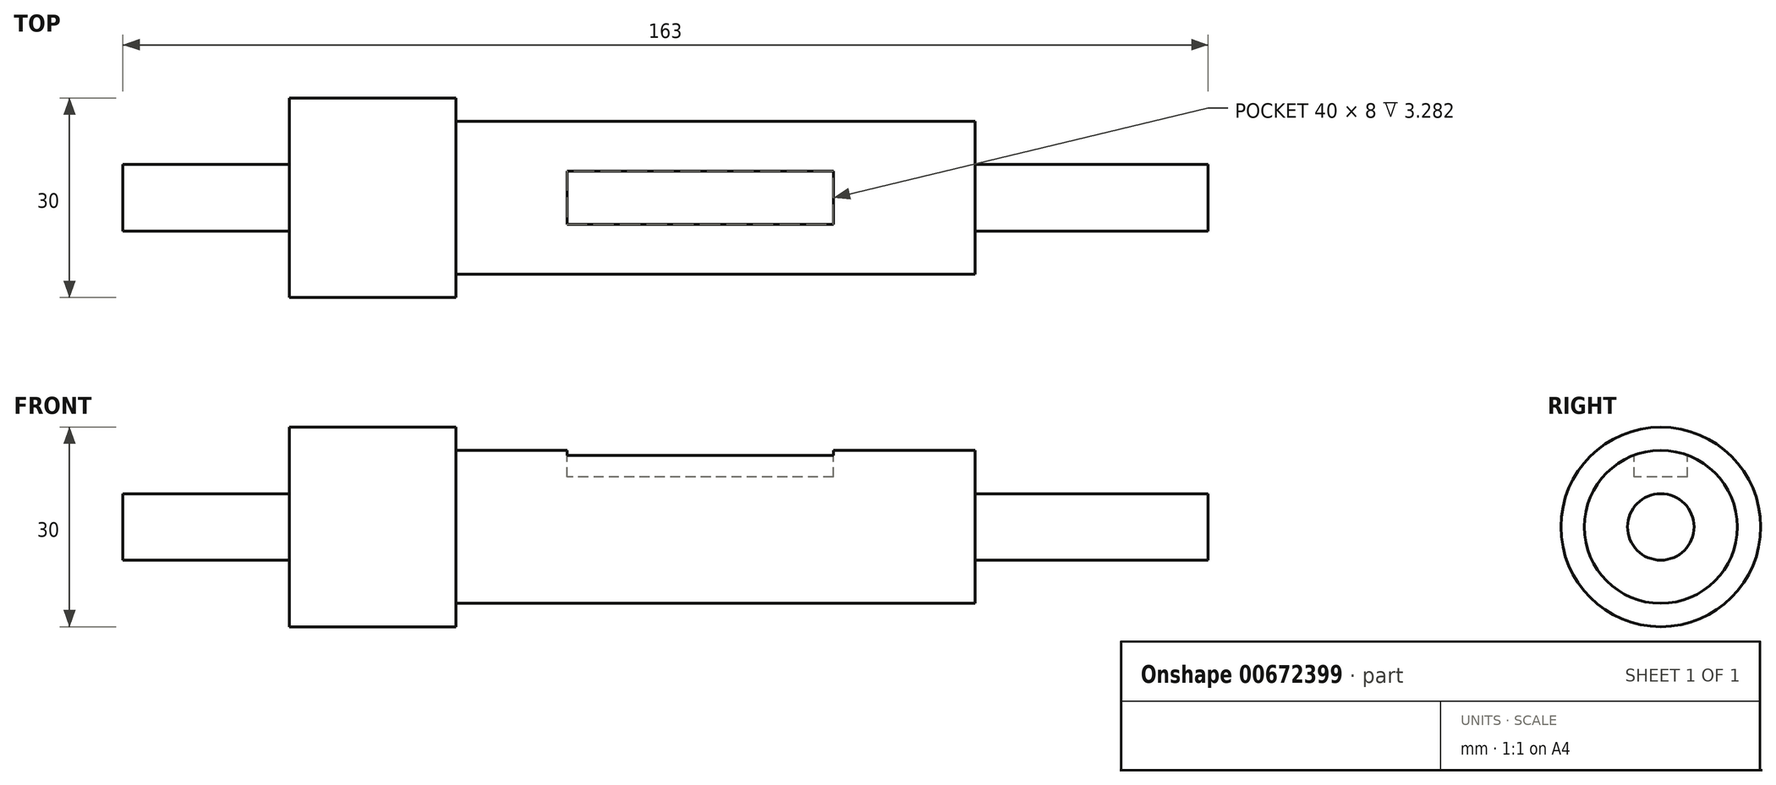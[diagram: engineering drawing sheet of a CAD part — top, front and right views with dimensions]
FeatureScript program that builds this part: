
annotation { "Feature Type Name" : "Feature", "Feature Type Description" : "" }
export const myFeature = defineFeature(function(context is Context, id is Id, definition is map)
    precondition{}
    {
        {
            var Q0;
            Q0=qCreatedBy(makeId("Right.planeOp"),FACE);
            var sketch = newSketch(context, id + "F0", { "sketchPlane" : qUnion([Q0])});
            skCircle(sketch, "E0", {"center": v(0, 0) * mm, "radius": 5 * mm});
            skSolve(sketch);
        }
        {
            var Q0;
            Q0 = qSketchRegion(id + "F0", true);
            extrude(context, id + "F1", {"entities" : qUnion([Q0]), "depth" : 35 * mm, "offsetDistance" : 25.4 * mm});
        }
        {
            var Q0;
            Q0=makeQuery(id+"F1.opExtrude","CAP_FACE",FACE,{"disambiguationData":[OSD([sQuery(id+"F0.wireOp",EDGE,"E0")])],"isStart":true});
            var sketch = newSketch(context, id + "F2", { "sketchPlane" : qUnion([Q0])});
            skCircle(sketch, "E1", {"center": v(0, 0) * mm, "radius": 11.5 * mm});
            skSolve(sketch);
        }
        {
            var Q0;
            Q0 = qSketchRegion(id + "F2", true);
            extrude(context, id + "F3", {"entities" : qUnion([Q0]), "operationType" : NewBodyOperationType.ADD, "depth" : 78 * mm, "offsetDistance" : 25.4 * mm});
        }
        {
            var Q0;
            Q0=makeQuery(id+"F3.opExtrude","CAP_FACE",FACE,{"disambiguationData":[OSD([sQuery(id+"F2.wireOp",EDGE,"E1")])],"isStart":false});
            var sketch = newSketch(context, id + "F4", { "sketchPlane" : qUnion([Q0])});
            skCircle(sketch, "E2", {"center": v(0, 0) * mm, "radius": 15 * mm});
            skSolve(sketch);
        }
        {
            var Q0;
            Q0 = qSketchRegion(id + "F4", true);
            extrude(context, id + "F5", {"entities" : qUnion([Q0]), "operationType" : NewBodyOperationType.ADD, "depth" : 25 * mm, "offsetDistance" : 25.4 * mm});
        }
        {
            var Q0;
            Q0=makeQuery(id+"F5.opExtrude","CAP_FACE",FACE,{"disambiguationData":[OSD([sQuery(id+"F4.wireOp",EDGE,"E2")])],"isStart":false});
            var sketch = newSketch(context, id + "F6", { "sketchPlane" : qUnion([Q0])});
            skCircle(sketch, "E3", {"center": v(0, 0) * mm, "radius": 5 * mm});
            skSolve(sketch);
        }
        {
            var Q0;
            Q0 = qSketchRegion(id + "F6", true);
            extrude(context, id + "F7", {"entities" : qUnion([Q0]), "operationType" : NewBodyOperationType.ADD, "depth" : 25 * mm, "offsetDistance" : 25.4 * mm});
        }
        {
            var Q0;
            Q0=qCreatedBy(makeId("Top.planeOp"),FACE);
            cPlane(context, id + "F8", {"entities" : qUnion([Q0]), "cplaneType" : CPlaneType.OFFSET, "offset" : 11.5 * mm, "width" : 152.4 * mm, "height" : 152.4 * mm});
        }
        {
            var Q0;
            Q0=qCreatedBy(id+"F8.planeOp",FACE);
            var sketch = newSketch(context, id + "F9", { "sketchPlane" : qUnion([Q0])});
            skLineSegment(sketch, "E4.bottom", {"start": v(-21.3, 4) * mm, "end": v(-61.3, 4) * mm});
            skLineSegment(sketch, "E4.top", {"start": v(-21.3, -4) * mm, "end": v(-61.3, -4) * mm});
            skLineSegment(sketch, "E4.left", {"start": v(-21.3, 4) * mm, "end": v(-21.3, -4) * mm});
            skLineSegment(sketch, "E4.right", {"start": v(-61.3, 4) * mm, "end": v(-61.3, -4) * mm});
            skPoint(sketch, "E4.middle", {"position": v(-41.3, 0) * mm});
            skSolve(sketch);
        }
        {
            var Q0;
            Q0 = qSketchRegion(id + "F9", true);
            extrude(context, id + "F10", {"entities" : qUnion([Q0]), "operationType" : NewBodyOperationType.REMOVE, "oppositeDirection" : true, "depth" : 4 * mm, "offsetDistance" : 25.4 * mm});
        }
    });
